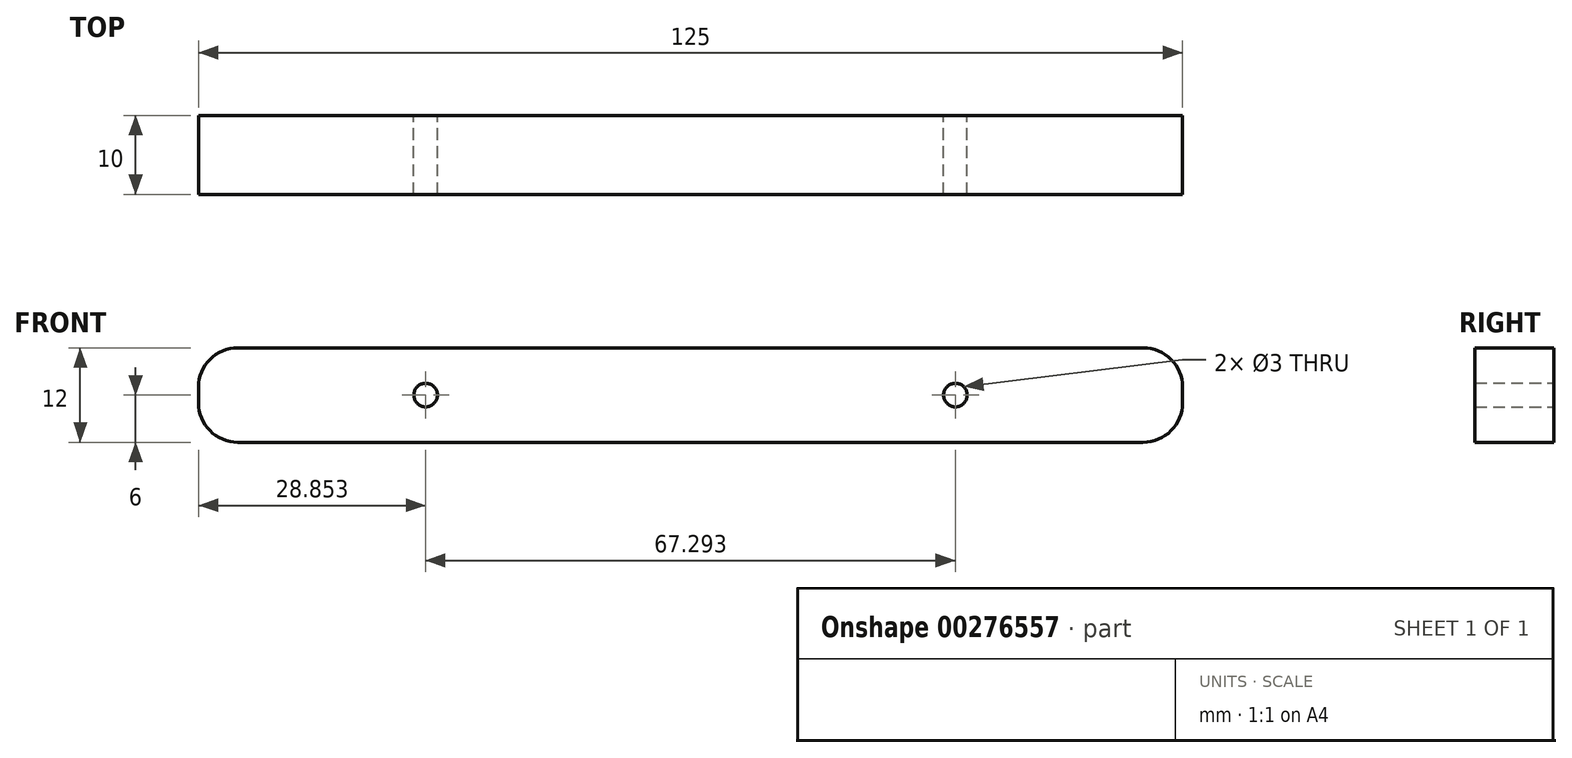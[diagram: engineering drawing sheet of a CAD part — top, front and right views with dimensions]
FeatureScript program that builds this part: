
annotation { "Feature Type Name" : "Feature", "Feature Type Description" : "" }
export const myFeature = defineFeature(function(context is Context, id is Id, definition is map)
    precondition{}
    {
        {
            var Q0;
            Q0=qCreatedBy(makeId("Front.planeOp"),FACE);
            var sketch = newSketch(context, id + "F0", { "sketchPlane" : qUnion([Q0])});
            skLineSegment(sketch, "E0.bottom", {"start": v(62.5, -6) * mm, "end": v(-62.5, -6) * mm});
            skLineSegment(sketch, "E0.top", {"start": v(62.5, 6) * mm, "end": v(-62.5, 6) * mm});
            skLineSegment(sketch, "E0.left", {"start": v(62.5, -6) * mm, "end": v(62.5, 6) * mm});
            skLineSegment(sketch, "E0.right", {"start": v(-62.5, -6) * mm, "end": v(-62.5, 6) * mm});
            skPoint(sketch, "E0.middle", {"position": v(0, 0) * mm});
            skCircle(sketch, "E1", {"center": v(-33.65, 0) * mm, "radius": 1.5 * mm});
            skCircle(sketch, "E2.MirrorC", {"center": v(33.65, 0) * mm, "radius": 1.5 * mm});
            skSolve(sketch);
        }
        {
            var Q0;
            Q0 = qSketchRegion(id + "F0", true);
            extrude(context, id + "F1", {"entities" : qUnion([Q0]), "depth" : 10 * mm, "offsetDistance" : 25 * mm});
        }
        {
            var Q0;
            Q0=makeQuery(id+"F1.opExtrude","SWEPT_EDGE",EDGE,{"disambiguationData":[OSD([sQuery(id+"F0.wireOp",EDGE,"E0.top"),sQuery(id+"F0.wireOp",EDGE,"E0.right")])]});
            var Q1;
            Q1=makeQuery(id+"F1.opExtrude","SWEPT_EDGE",EDGE,{"disambiguationData":[OSD([sQuery(id+"F0.wireOp",EDGE,"E0.bottom"),sQuery(id+"F0.wireOp",EDGE,"E0.right")])]});
            var Q2;
            Q2=makeQuery(id+"F1.opExtrude","SWEPT_EDGE",EDGE,{"disambiguationData":[OSD([sQuery(id+"F0.wireOp",EDGE,"E0.top"),sQuery(id+"F0.wireOp",EDGE,"E0.left")])]});
            var Q3;
            Q3=makeQuery(id+"F1.opExtrude","SWEPT_EDGE",EDGE,{"disambiguationData":[OSD([sQuery(id+"F0.wireOp",EDGE,"E0.bottom"),sQuery(id+"F0.wireOp",EDGE,"E0.left")])]});
            fillet(context, id + "F2", {"entities" : qUnion([Q0, Q1, Q2, Q3]), "tangentPropagation" : true, "radius" : 5 * mm, "defaultsChanged" : false, "vertexSettings" : [], "allowEdgeOverflow" : false});
        }
    });
